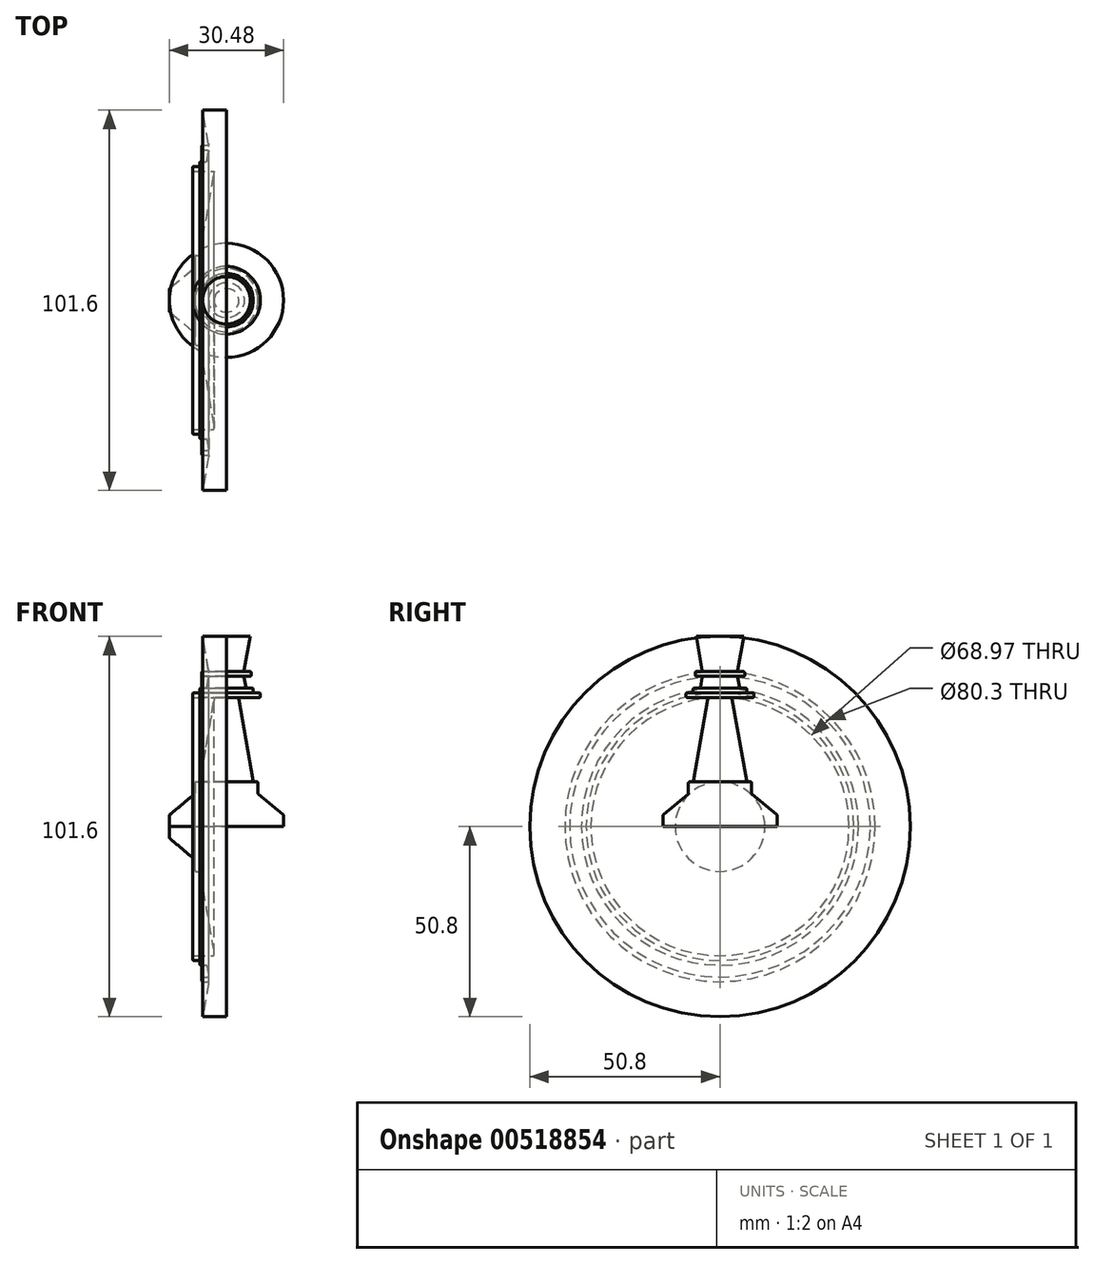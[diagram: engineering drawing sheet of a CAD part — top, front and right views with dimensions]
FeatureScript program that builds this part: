
annotation { "Feature Type Name" : "Feature", "Feature Type Description" : "" }
export const myFeature = defineFeature(function(context is Context, id is Id, definition is map)
    precondition{}
    {
        {
            var Q0;
            Q0=qCreatedBy(makeId("Front.planeOp"),FACE);
            var sketch = newSketch(context, id + "F0", { "sketchPlane" : qUnion([Q0])});
            skLineSegment(sketch, "E0.bottom", {"start": v(0, 0) * mm, "end": v(-15.24, 0) * mm});
            skLineSegment(sketch, "E0.top", {"start": v(0, 50.8) * mm, "end": v(-6.35, 50.8) * mm});
            skLineSegment(sketch, "E0.left", {"start": v(0, 0) * mm, "end": v(0, 50.8) * mm});
            skLineSegment(sketch, "E1", {"start": v(-15.24, 0) * mm, "end": v(-15.24, 2.93) * mm});
            skLineSegment(sketch, "E2", {"start": v(-15.13, 3.18) * mm, "end": v(-8.54, 8.7) * mm});
            skLineSegment(sketch, "E3", {"start": v(-8.43, 8.94) * mm, "end": v(-8.43, 11.65) * mm});
            skLineSegment(sketch, "E4", {"start": v(-8.11, 11.97) * mm, "end": v(-7.43, 11.97) * mm});
            skLineSegment(sketch, "E5", {"start": v(-7.11, 12.23) * mm, "end": v(-3.26, 34.11) * mm});
            skLineSegment(sketch, "E6", {"start": v(-3.57, 34.48) * mm, "end": v(-8.74, 34.48) * mm});
            skLineSegment(sketch, "E7", {"start": v(-9.06, 34.8) * mm, "end": v(-9.06, 35.44) * mm});
            skLineSegment(sketch, "E8", {"start": v(-8.74, 35.75) * mm, "end": v(-7.47, 35.75) * mm});
            skLineSegment(sketch, "E9", {"start": v(-7.15, 36.07) * mm, "end": v(-7.15, 36.7) * mm});
            skLineSegment(sketch, "E10", {"start": v(-6.83, 37.02) * mm, "end": v(-5.51, 37.02) * mm});
            skLineSegment(sketch, "E11", {"start": v(-5.2, 37.29) * mm, "end": v(-4.76, 39.78) * mm});
            skLineSegment(sketch, "E12", {"start": v(-5.07, 40.15) * mm, "end": v(-6.28, 40.15) * mm});
            skLineSegment(sketch, "E13", {"start": v(-6.6, 40.47) * mm, "end": v(-6.6, 41.1) * mm});
            skLineSegment(sketch, "E14", {"start": v(-6.28, 41.42) * mm, "end": v(-5.07, 41.42) * mm});
            skLineSegment(sketch, "E15", {"start": v(-4.76, 41.8) * mm, "end": v(-6.35, 50.8) * mm});
            skPoint(sketch, "E16.visualSharp", {"position": v(-15.24, 3.08) * mm});
            skArc(sketch, "E16.filletArc", {"start": v(-15.13, 3.18) * mm, "mid": v(-15.21, 3.07) * mm, "end": v(-15.24, 2.93) * mm});
            skPoint(sketch, "E17.visualSharp", {"position": v(-8.43, 8.8) * mm});
            skArc(sketch, "E17.filletArc", {"start": v(-8.54, 8.7) * mm, "mid": v(-8.46, 8.8) * mm, "end": v(-8.43, 8.94) * mm});
            skPoint(sketch, "E18.visualSharp", {"position": v(-3.2, 34.48) * mm});
            skArc(sketch, "E18.filletArc", {"start": v(-3.26, 34.11) * mm, "mid": v(-3.33, 34.37) * mm, "end": v(-3.57, 34.48) * mm});
            skPoint(sketch, "E19.visualSharp", {"position": v(-8.43, 11.97) * mm});
            skArc(sketch, "E19.filletArc", {"start": v(-8.11, 11.97) * mm, "mid": v(-8.34, 11.88) * mm, "end": v(-8.43, 11.65) * mm});
            skPoint(sketch, "E20.visualSharp", {"position": v(-7.16, 11.97) * mm});
            skArc(sketch, "E20.filletArc", {"start": v(-7.43, 11.97) * mm, "mid": v(-7.22, 12.04) * mm, "end": v(-7.11, 12.23) * mm});
            skPoint(sketch, "E21.visualSharp", {"position": v(-9.06, 34.48) * mm});
            skArc(sketch, "E21.filletArc", {"start": v(-9.06, 34.8) * mm, "mid": v(-8.96, 34.58) * mm, "end": v(-8.74, 34.48) * mm});
            skPoint(sketch, "E22.visualSharp", {"position": v(-9.06, 35.75) * mm});
            skArc(sketch, "E22.filletArc", {"start": v(-8.74, 35.75) * mm, "mid": v(-8.96, 35.66) * mm, "end": v(-9.06, 35.44) * mm});
            skPoint(sketch, "E23.visualSharp", {"position": v(-7.15, 35.75) * mm});
            skArc(sketch, "E23.filletArc", {"start": v(-7.47, 35.75) * mm, "mid": v(-7.25, 35.85) * mm, "end": v(-7.15, 36.07) * mm});
            skPoint(sketch, "E24.visualSharp", {"position": v(-7.15, 37.02) * mm});
            skArc(sketch, "E24.filletArc", {"start": v(-6.83, 37.02) * mm, "mid": v(-7.06, 36.93) * mm, "end": v(-7.15, 36.7) * mm});
            skPoint(sketch, "E25.visualSharp", {"position": v(-5.25, 37.02) * mm});
            skArc(sketch, "E25.filletArc", {"start": v(-5.51, 37.02) * mm, "mid": v(-5.3, 37.1) * mm, "end": v(-5.2, 37.29) * mm});
            skPoint(sketch, "E26.visualSharp", {"position": v(-4.7, 40.15) * mm});
            skArc(sketch, "E26.filletArc", {"start": v(-4.76, 39.78) * mm, "mid": v(-4.83, 40.04) * mm, "end": v(-5.07, 40.15) * mm});
            skPoint(sketch, "E27.visualSharp", {"position": v(-6.6, 40.15) * mm});
            skArc(sketch, "E27.filletArc", {"start": v(-6.6, 40.47) * mm, "mid": v(-6.5, 40.24) * mm, "end": v(-6.28, 40.15) * mm});
            skPoint(sketch, "E28.visualSharp", {"position": v(-6.6, 41.42) * mm});
            skArc(sketch, "E28.filletArc", {"start": v(-6.28, 41.42) * mm, "mid": v(-6.5, 41.33) * mm, "end": v(-6.6, 41.1) * mm});
            skPoint(sketch, "E29.visualSharp", {"position": v(-4.7, 41.42) * mm});
            skArc(sketch, "E29.filletArc", {"start": v(-5.07, 41.42) * mm, "mid": v(-4.83, 41.53) * mm, "end": v(-4.76, 41.8) * mm});
            skSolve(sketch);
        }
        {
            var Q0;
            Q0=makeQuery(id+"F0.imprint","IMPRINT",FACE,{"disambiguationData":[TD([[makeQuery(id+"F0.imprint","IMPRINT",EDGE,{"derivedFrom":sQuery(id+"F0.wireOp",EDGE,"E0.bottom")}),-1.0]])]});
            var Q1;
            Q1=sQuery(id+"F0.wireOp",EDGE,"E0.bottom");
            revolve(context, id + "F1", {"entities" : qUnion([Q0]), "axis" : qUnion([Q1]), "revolveType" : RevolveType.FULL});
        }
        {
            var Q0;
            Q0=makeQuery(id+"F0.imprint","IMPRINT",FACE,{"disambiguationData":[TD([[makeQuery(id+"F0.imprint","IMPRINT",EDGE,{"derivedFrom":sQuery(id+"F0.wireOp",EDGE,"E0.bottom")}),-1.0]])]});
            var Q1;
            Q1=sQuery(id+"F0.wireOp",EDGE,"E0.left");
            revolve(context, id + "F2", {"entities" : qUnion([Q0]), "axis" : qUnion([Q1]), "revolveType" : RevolveType.FULL});
        }
    });
